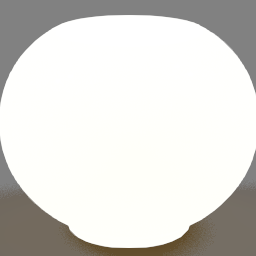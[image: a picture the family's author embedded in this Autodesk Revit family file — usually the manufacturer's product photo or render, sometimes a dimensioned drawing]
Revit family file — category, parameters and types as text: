
# Revit family: 3-5054-xx-xx Axiom Wall Sconce
name_source: partatom
category: Luminarias
units: mm (PartAtom-declared; Revit-internal decimal feet)

## family parameters
Anfitrión = Muro
Compartido = No
Corte con vacíos al cargar = No
Cota de conector redondo = Diámetro de uso
Número OmniClass = 23.80.70.00
Origen de luz = Sí
Punto de cálculo de habitación = No
Siempre vertical = Sí
Tipo de pieza = Normal
Título OmniClass = Lighting

## types (2) — shared parameters
Archivo de red fotométrica = 3-5054-15 Axiom 5LT.ies
Cambio de temperatura de color de luz atenuada = <Ninguno>
Comentarios de vataje = 1 x 12.0 W at 120 V
Diffuser = Ice Acrylic
Fabricante = Oxygen Lighting and Fans
Filtro de color = 16777215
Lámpara = LED Array
Modelo = 3-5054-xx / Axiom Wall Sconce
References = Ref. 3 = 120 V / Ref. 37 = 277 V
URL = www.oxygenlighting.com
Voltage = 120 V
Voltage Input = 120 V or 277 V - 50/60 Hz
Ángulo de inclinación = 90.00°
zero-valued in all types: Elevación por defecto

## per-type parameters (varying)
| type | Metal Finish 1 |
| 3-5054-15 / Black - ice acrylic | 15 - Black |
| 3-5054-40 / Aged Brass - Ice Acrylic | 40 - Aged Brass |

## geometry (parser evidence)
native form markers: Sweep x4
no freeform markers — native parametric forms only
